# Revit family: Napkin_Disposal-Wall_Mounted-Bradley_Corp-4781-4791
name_source: partatom
category: Specialty Equipment
units: mm (PartAtom-declared; Revit-internal decimal feet)

## family parameters
Cut with Voids When Loaded = No
Host = Face
OmniClass Number = 23.40.20.21.24
OmniClass Title = Sanitary Napkin and Tampon Dispensers, Disposal Units
Part Type = Normal
Room Calculation Point = No
Round Connector Dimension = Use Diameter
Shared = No

## types (2) — shared parameters
ADA Compliant = Yes
Assembly Code = C1030200
Default Elevation = 26 "
Depth = 4.25 "
Height = 11.375 "
Housing Material = Metal - Bradley Corp - Stainless Steel - Satin
LEED Credit = 0
Low Emitting Material = No
Manufacturer = Bradley Corporation
MasterFormat Number = 10 28 00
MasterFormat Title = Toilet, Bath, and Laundry Accessories
OmniClass Table 21 Number = 21-03 10 90 40
OmniClass Table 21 Title = Toilet, Bath, and Laundry Accessories
OmniClass Table 23 Number = 23.40.20.21.24
OmniClass Table 23 Title = Sanitary Napkin and Tampon Dispensers, Disposal Units
Product Page URL = https://www.bradleycorp.com
Product Tech Data URL - English = https://www.bradleycorp.com
Specifications URL = http://www.bradleycorp.com
URL = http://www.bradleycorp.com
Version = 1.0
Warranty Information = Complete Unit 1 Year Warranty. This Warranty does not cover installation or any other labor charges and does not apply to any units which have been damaged by abuse, improper installation, imporper maintanence, or altered in any way.
Width = 8 "
zero-valued in all types: Percentage of Recycled Content, z Offset From Wall

## per-type parameters (varying)
| type | Description | z Left Ref Offset | z Shelf is Visible |
| 4791-11 | Surface Mounted Napkin Disposal with Shelf | 8 " | Yes |
| 4781-11 | Surface Mounted Napkin Disposal | 0 " | No |

note: column(s) folded — value = type name in every type: Model

## geometry (parser evidence)
native form markers: Sweep x2
no freeform markers — native parametric forms only
